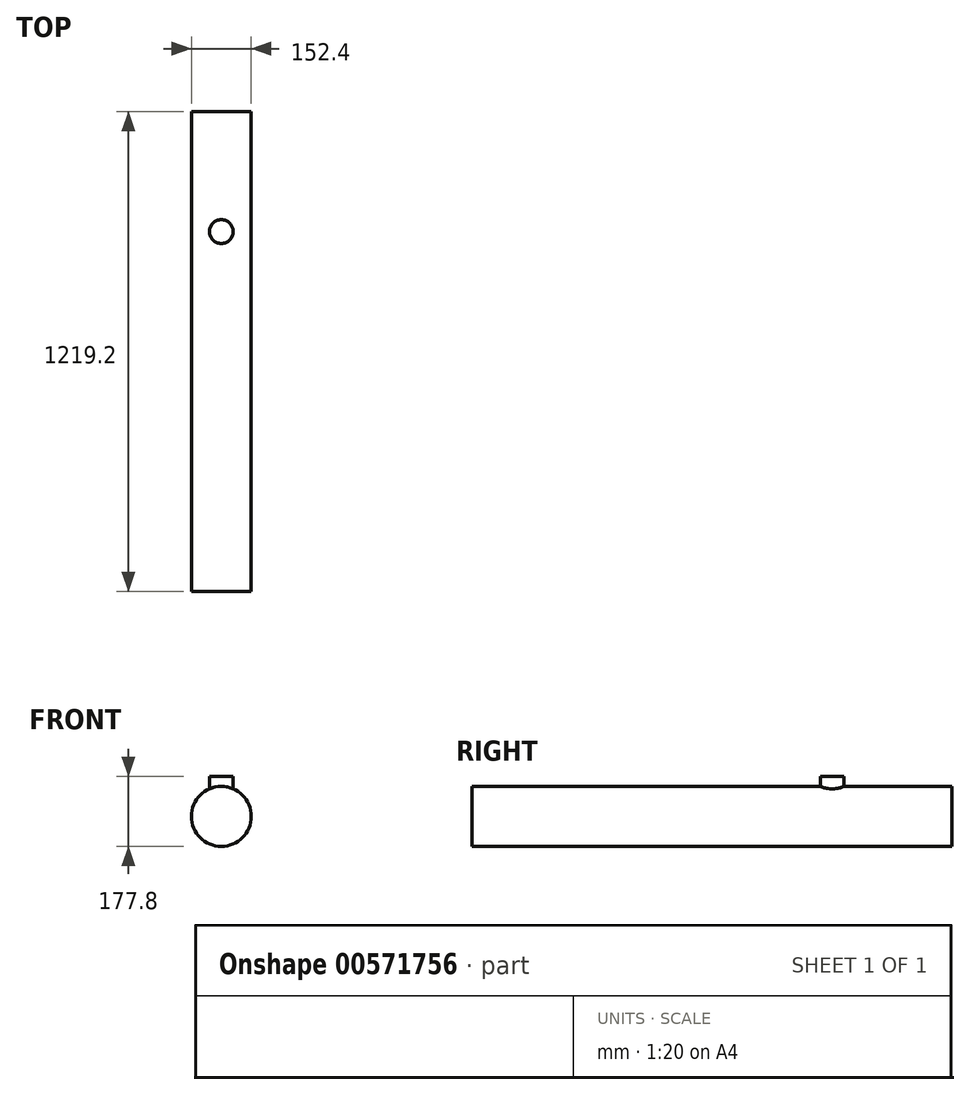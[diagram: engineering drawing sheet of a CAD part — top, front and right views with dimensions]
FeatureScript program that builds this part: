
annotation { "Feature Type Name" : "Feature", "Feature Type Description" : "" }
export const myFeature = defineFeature(function(context is Context, id is Id, definition is map)
    precondition{}
    {
        {
            var Q0;
            Q0=qCreatedBy(makeId("Front.planeOp"),FACE);
            var sketch = newSketch(context, id + "F0", { "sketchPlane" : qUnion([Q0])});
            skCircle(sketch, "E0", {"center": v(0, 0) * mm, "radius": 76.2 * mm});
            skSolve(sketch);
        }
        {
            var Q0;
            Q0=makeQuery(id+"F0.imprint","IMPRINT",FACE,{"disambiguationData":[TD([[makeQuery(id+"F0.imprint","IMPRINT",EDGE,{"derivedFrom":sQuery(id+"F0.wireOp",EDGE,"E0")}),1.0]])]});
            extrude(context, id + "F1", {"entities" : qUnion([Q0]), "depth" : 914.4 * mm, "offsetDistance" : 25.4 * mm, "hasSecondDirection" : true, "secondDirectionOppositeDirection" : true, "secondDirectionDepth" : 304.8 * mm});
        }
        {
            var Q0;
            Q0=qCreatedBy(makeId("Top.planeOp"),FACE);
            var sketch = newSketch(context, id + "F2", { "sketchPlane" : qUnion([Q0])});
            skCircle(sketch, "E1", {"center": v(0, 0) * mm, "radius": 30.23 * mm});
            skSolve(sketch);
        }
        {
            var Q0;
            Q0 = qSketchRegion(id + "F2", true);
            extrude(context, id + "F3", {"entities" : qUnion([Q0]), "operationType" : NewBodyOperationType.ADD, "depth" : 101.6 * mm, "offsetDistance" : 25.4 * mm});
        }
    });
